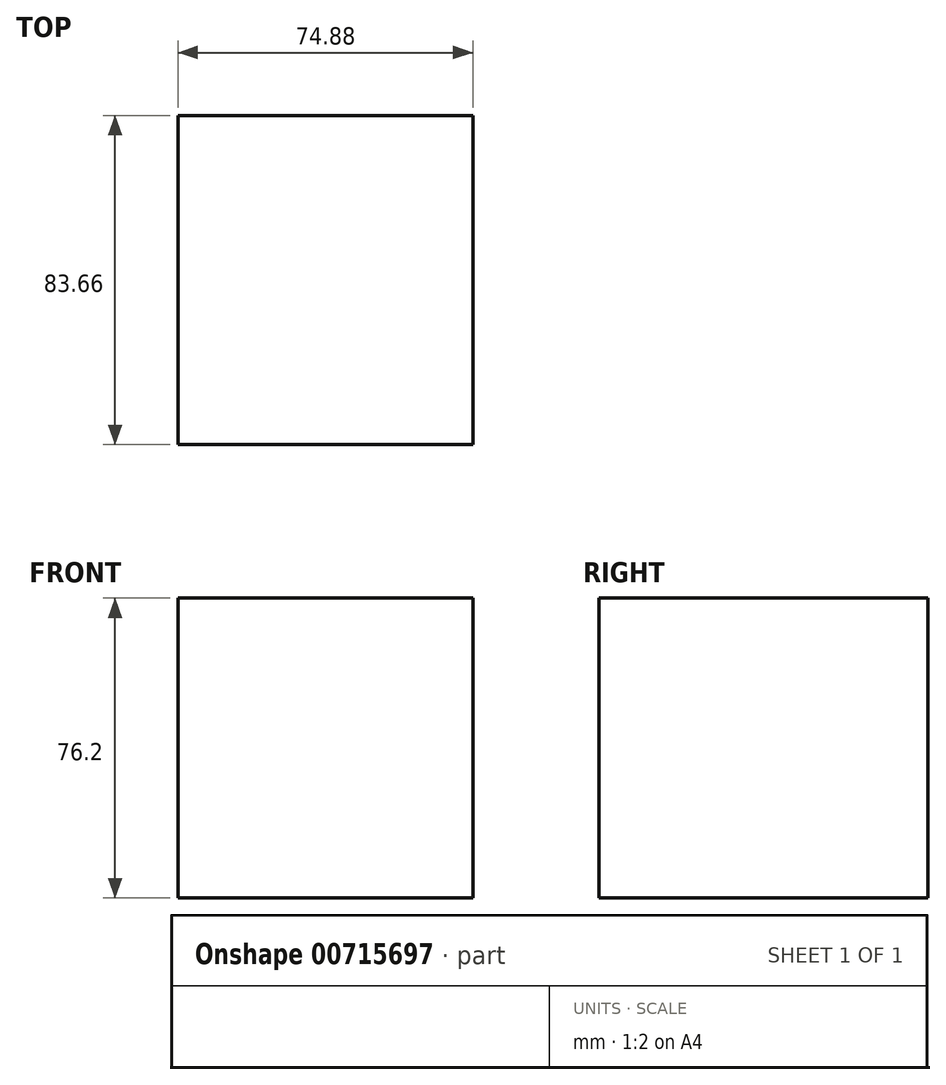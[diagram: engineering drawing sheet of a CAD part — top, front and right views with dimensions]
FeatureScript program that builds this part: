
annotation { "Feature Type Name" : "Feature", "Feature Type Description" : "" }
export const myFeature = defineFeature(function(context is Context, id is Id, definition is map)
    precondition{}
    {
        {
            var Q0;
            Q0=qCreatedBy(makeId("Top.planeOp"),FACE);
            var sketch = newSketch(context, id + "F0", { "sketchPlane" : qUnion([Q0])});
            skLineSegment(sketch, "E0.bottom", {"start": v(-24.99, 41.83) * mm, "end": v(49.9, 41.83) * mm});
            skLineSegment(sketch, "E0.top", {"start": v(-24.99, -41.83) * mm, "end": v(49.9, -41.83) * mm});
            skLineSegment(sketch, "E0.left", {"start": v(-24.99, 41.83) * mm, "end": v(-24.99, -41.83) * mm});
            skLineSegment(sketch, "E0.right", {"start": v(49.9, 41.83) * mm, "end": v(49.9, -41.83) * mm});
            skPoint(sketch, "E0.middle", {"position": v(12.45, 0) * mm});
            skSolve(sketch);
        }
        {
            var Q0;
            Q0 = qSketchRegion(id + "F0", true);
            extrude(context, id + "F1", {"entities" : qUnion([Q0]), "depth" : 76.2 * mm, "offsetDistance" : 25.4 * mm});
        }
    });
